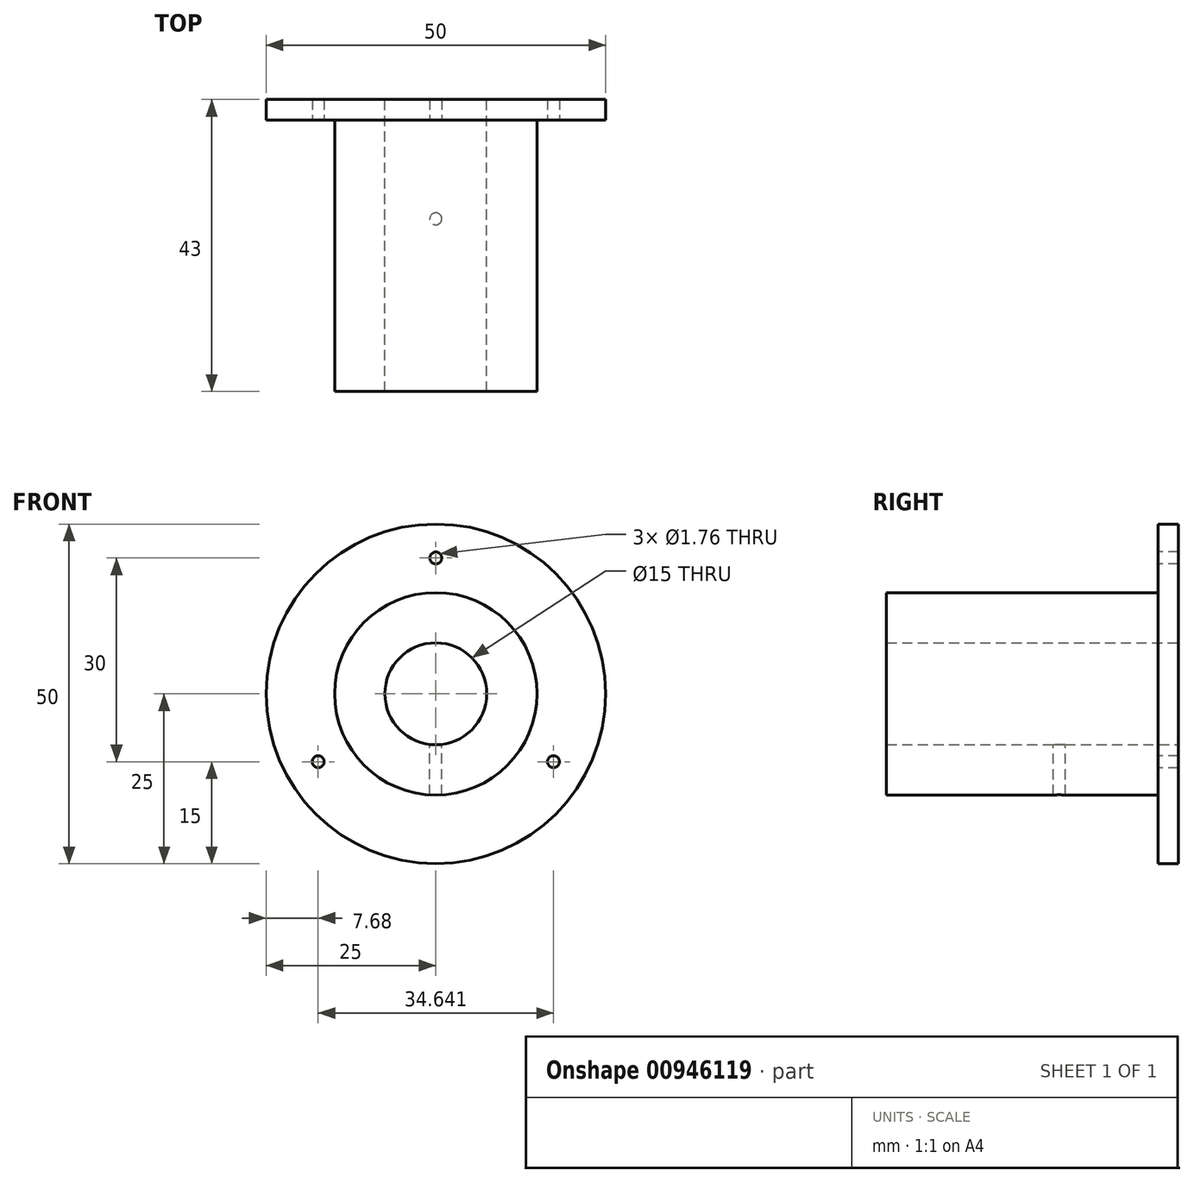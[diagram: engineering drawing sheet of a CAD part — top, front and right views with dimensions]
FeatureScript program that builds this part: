
annotation { "Feature Type Name" : "Feature", "Feature Type Description" : "" }
export const myFeature = defineFeature(function(context is Context, id is Id, definition is map)
    precondition{}
    {
        {
            var Q0;
            Q0=qCreatedBy(makeId("Front.planeOp"),FACE);
            var sketch = newSketch(context, id + "F0", { "sketchPlane" : qUnion([Q0])});
            skCircle(sketch, "E0", {"center": v(0, 0) * mm, "radius": 14.9 * mm});
            skCircle(sketch, "E1", {"center": v(0, 0) * mm, "radius": 7.5 * mm});
            skCircle(sketch, "E2", {"center": v(0, 0) * mm, "radius": 25 * mm});
            skCircle(sketch, "E3", {"center": v(0, 20) * mm, "radius": 0.88 * mm});
            skCircle(sketch, "E4.1.0", {"center": v(-17.32, -10) * mm, "radius": 0.88 * mm});
            skCircle(sketch, "E4.2.0", {"center": v(17.32, -10) * mm, "radius": 0.88 * mm});
            skSolve(sketch);
        }
        {
            var Q0;
            Q0=makeQuery(id+"F0.imprint","IMPRINT",FACE,{"disambiguationData":[TD([[makeQuery(id+"F0.imprint","IMPRINT",EDGE,{"derivedFrom":sQuery(id+"F0.wireOp",EDGE,"E0")}),1.0]])]});
            extrude(context, id + "F1", {"entities" : qUnion([Q0]), "depth" : 40 * mm});
        }
        {
            var Q0;
            Q0=makeQuery(id+"F0.imprint","IMPRINT",FACE,{"disambiguationData":[TD([[makeQuery(id+"F0.imprint","IMPRINT",EDGE,{"derivedFrom":sQuery(id+"F0.wireOp",EDGE,"E0")}),-1.0]])]});
            var Q1;
            Q1=makeQuery(id+"F0.imprint","IMPRINT",FACE,{"disambiguationData":[TD([[makeQuery(id+"F0.imprint","IMPRINT",EDGE,{"derivedFrom":sQuery(id+"F0.wireOp",EDGE,"E0")}),1.0]])]});
            extrude(context, id + "F2", {"entities" : qUnion([Q0, Q1]), "operationType" : NewBodyOperationType.ADD, "oppositeDirection" : true, "depth" : 3 * mm});
        }
        {
            var Q0;
            Q0=qCreatedBy(makeId("Top.planeOp"),FACE);
            var sketch = newSketch(context, id + "F3", { "sketchPlane" : qUnion([Q0])});
            skCircle(sketch, "E5", {"center": v(0, -14.56) * mm, "radius": 0.88 * mm});
            skSolve(sketch);
        }
        {
            var Q0;
            Q0=qSketchRegion(id+"F3",true);
            extrude(context, id + "F4", {"entities" : qUnion([Q0]), "operationType" : NewBodyOperationType.REMOVE, "oppositeDirection" : true, "depth" : 25 * mm});
        }
    });
